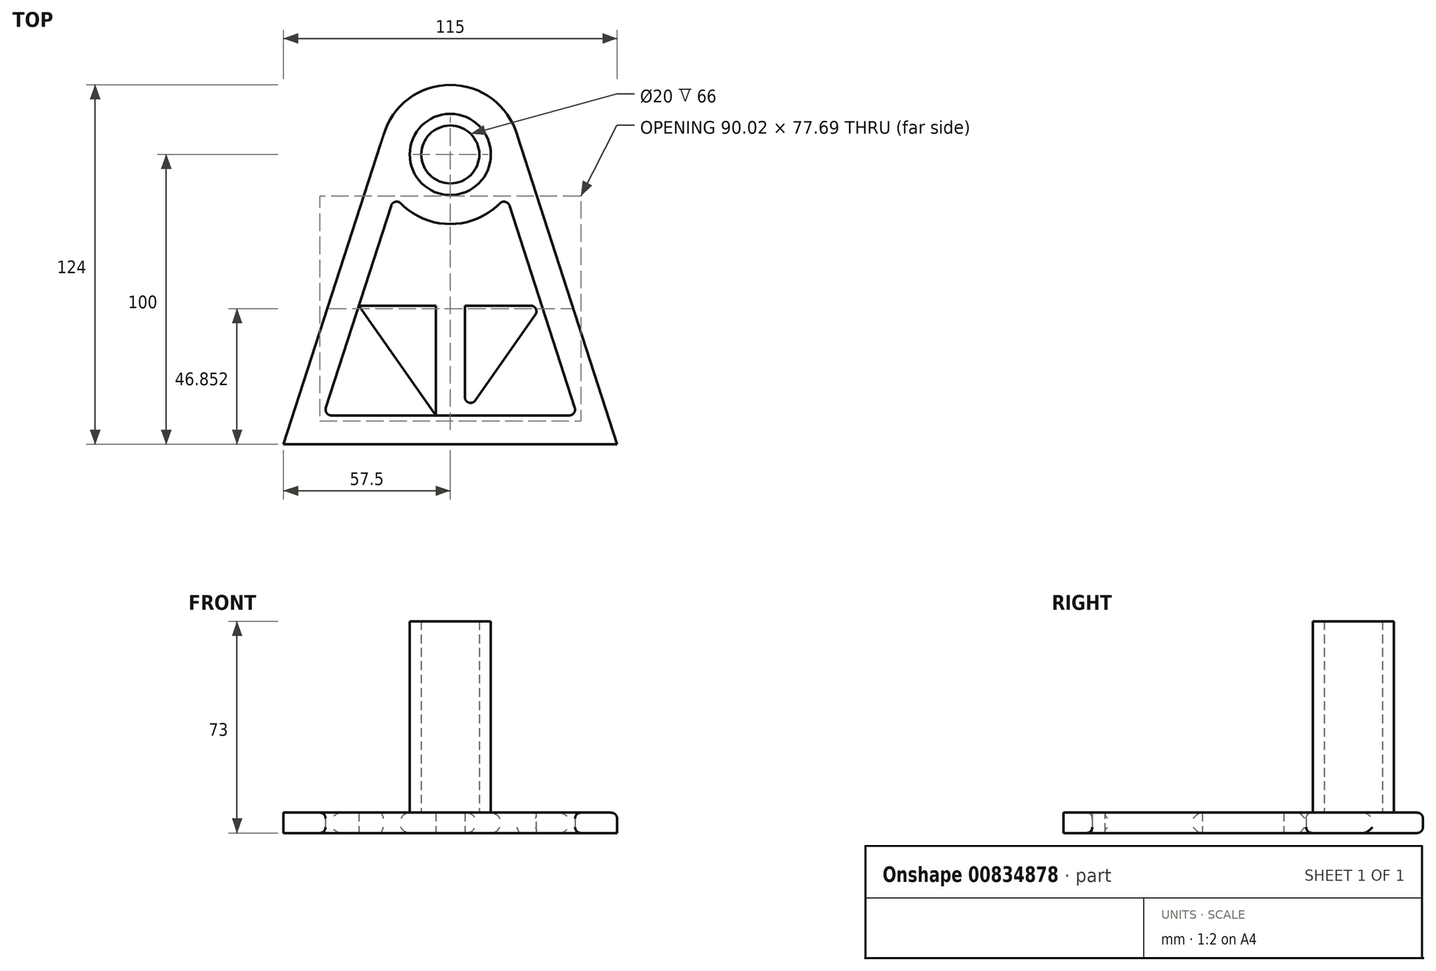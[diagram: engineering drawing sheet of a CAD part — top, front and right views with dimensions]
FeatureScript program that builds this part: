
annotation { "Feature Type Name" : "Feature", "Feature Type Description" : "" }
export const myFeature = defineFeature(function(context is Context, id is Id, definition is map)
    precondition{}
    {
        {
            var Q0;
            Q0=qCreatedBy(makeId("Top.planeOp"),FACE);
            var sketch = newSketch(context, id + "F0", { "sketchPlane" : qUnion([Q0])});
            skCircle(sketch, "E0", {"center": v(0, 0) * mm, "radius": 14 * mm});
            skLineSegment(sketch, "E1", {"start": v(0, 0) * mm, "end": v(0, -100) * mm});
            skCircle(sketch, "E2", {"center": v(0, 0) * mm, "radius": 24 * mm});
            skLineSegment(sketch, "E3", {"start": v(0, -100) * mm, "end": v(-57.5, -100) * mm});
            skLineSegment(sketch, "E4", {"start": v(-57.5, -100) * mm, "end": v(57.5, -100) * mm});
            skLineSegment(sketch, "E5", {"start": v(-23.06, 6.66) * mm, "end": v(-57.5, -100) * mm});
            skLineSegment(sketch, "E6", {"start": v(23.06, 6.66) * mm, "end": v(57.5, -100) * mm});
            skCircle(sketch, "E7", {"center": v(0, 0) * mm, "radius": 10 * mm});
            skLineSegment(sketch, "E8", {"start": v(24.7, -100) * mm, "end": v(24.7, -90) * mm});
            skLineSegment(sketch, "E9", {"start": v(24.7, -90) * mm, "end": v(-43.76, -90) * mm});
            skLineSegment(sketch, "E10", {"start": v(-43.76, -90) * mm, "end": v(-53.28, -86.93) * mm});
            skLineSegment(sketch, "E11", {"start": v(-43.76, -90) * mm, "end": v(-43.76, -100) * mm});
            skLineSegment(sketch, "E12", {"start": v(-43.76, -100) * mm, "end": v(-43.76, -90) * mm});
            skLineSegment(sketch, "E13", {"start": v(-43.76, -90) * mm, "end": v(-19.3, -14.26) * mm});
            skLineSegment(sketch, "E14", {"start": v(24.7, -90) * mm, "end": v(43.76, -90) * mm});
            skLineSegment(sketch, "E15", {"start": v(43.76, -90) * mm, "end": v(53.28, -86.93) * mm});
            skLineSegment(sketch, "E16", {"start": v(43.76, -90) * mm, "end": v(19.3, -14.26) * mm});
            skLineSegment(sketch, "E17", {"start": v(-19.83, -15.9) * mm, "end": v(-29.35, -12.82) * mm});
            skLineSegment(sketch, "E18", {"start": v(0, -90) * mm, "end": v(-5, -90) * mm});
            skLineSegment(sketch, "E19", {"start": v(-5, -90) * mm, "end": v(-31.53, -52.13) * mm});
            skLineSegment(sketch, "E20", {"start": v(0, -90) * mm, "end": v(5, -90) * mm});
            skLineSegment(sketch, "E21", {"start": v(5, -90) * mm, "end": v(31.53, -52.13) * mm});
            skLineSegment(sketch, "E22", {"start": v(5, -90) * mm, "end": v(5, -52.13) * mm});
            skLineSegment(sketch, "E23", {"start": v(-5, -52.13) * mm, "end": v(-5, -90) * mm});
            skLineSegment(sketch, "E24", {"start": v(-5, -52.13) * mm, "end": v(-31.53, -52.13) * mm});
            skLineSegment(sketch, "E25", {"start": v(5, -52.13) * mm, "end": v(31.53, -52.13) * mm});
            skLineSegment(sketch, "E26", {"start": v(-5, -42.32) * mm, "end": v(-28.37, -42.32) * mm});
            skLineSegment(sketch, "E27", {"start": v(5, -41.98) * mm, "end": v(28.26, -41.98) * mm});
            skLineSegment(sketch, "E28", {"start": v(5, -41.98) * mm, "end": v(5, -23.47) * mm});
            skLineSegment(sketch, "E29", {"start": v(-5, -42.32) * mm, "end": v(-5, -23.47) * mm});
            skSolve(sketch);
        }
        {
            var Q0;
            Q0 = qSketchRegion(id + "F0", true);
            var Q1;
            Q1=makeQuery(id+"F0.imprint","IMPRINT",FACE,{"disambiguationData":[TD([[makeQuery(id+"F0.imprint","IMPRINT",EDGE,{"derivedFrom":sQuery(id+"F0.wireOp",EDGE,"E19")}),-1.0]])]});
            var Q2;
            Q2=makeQuery(id+"F0.imprint","IMPRINT",FACE,{"disambiguationData":[TD([[makeQuery(id+"F0.imprint","IMPRINT",EDGE,{"derivedFrom":sQuery(id+"F0.wireOp",EDGE,"E21")}),1.0]])]});
            var Q3;
            {var subQ0=sQuery(id+"F0.wireOp",EDGE,"E20");Q3=makeQuery(id+"F0.imprint","IMPRINT",FACE,{"disambiguationData":[TD([[makeQuery(id+"F0.imprint","IMPRINT",EDGE,{"derivedFrom":subQ0}),1.0]])]});}
            var Q4;
            {var subQ0=sQuery(id+"F0.wireOp",EDGE,"E18");Q4=makeQuery(id+"F0.imprint","IMPRINT",FACE,{"disambiguationData":[TD([[makeQuery(id+"F0.imprint","IMPRINT",EDGE,{"derivedFrom":subQ0}),-1.0]])]});}
            var Q5;
            Q5=makeQuery(id+"F0.imprint","IMPRINT",FACE,{"disambiguationData":[TD([[makeQuery(id+"F0.imprint","IMPRINT",EDGE,{"derivedFrom":sQuery(id+"F0.wireOp",EDGE,"E7")}),1.0]])]});
            var Q6;
            Q6=makeQuery(id+"F0.imprint","IMPRINT",FACE,{"disambiguationData":[TD([[makeQuery(id+"F0.imprint","IMPRINT",EDGE,{"derivedFrom":sQuery(id+"F0.wireOp",EDGE,"E0")}),1.0]])]});
            extrude(context, id + "F1", {"entities" : qUnion([Q0, Q1, Q2, Q3, Q4, Q5, Q6]), "depth" : 7 * mm, "offsetDistance" : 25 * mm});
        }
        {
            var Q0;
            Q0=makeQuery(id+"F0.imprint","IMPRINT",FACE,{"disambiguationData":[TD([[makeQuery(id+"F0.imprint","IMPRINT",EDGE,{"derivedFrom":sQuery(id+"F0.wireOp",EDGE,"E0")}),1.0]])]});
            extrude(context, id + "F2", {"entities" : qUnion([Q0]), "operationType" : NewBodyOperationType.ADD, "depth" : 73 * mm, "offsetDistance" : 25 * mm});
        }
        {
            var Q0;
            Q0=makeQuery(id+"F1.opExtrude","CAP_EDGE",EDGE,{"disambiguationData":[OSD([sQuery(id+"F0.wireOp",EDGE,"E28")])],"isStart":false});
            var Q1;
            {var subQ0=sQuery(id+"F0.wireOp",EDGE,"E13");var subQ1=makeQuery(id+"F0.imprint","INTERSECT",VERTEX,{"derivedFrom":[subQ0,sQuery(id+"F0.wireOp",EDGE,"E17")]});Q1=makeQuery(id+"F1.opExtrude","SWEPT_FACE",FACE,{"disambiguationData":[OSD([subQ0]),TDD([makeQuery(id+"F0.imprint","IMPRINT",EDGE,{"disambiguationData":[TD([[subQ1,1.0]])],"derivedFrom":subQ0}),makeQuery(id+"F0.imprint","IMPRINT",EDGE,{"disambiguationData":[TD([[makeQuery(id+"F0.imprint","INTERSECT",VERTEX,{"derivedFrom":[sQuery(id+"F0.wireOp",EDGE,"E2"),subQ0]}),1.0]])],"derivedFrom":subQ0})])]});}
            var Q2;
            Q2=makeQuery(id+"F1.opExtrude","SWEPT_FACE",FACE,{"disambiguationData":[OSD([sQuery(id+"F0.wireOp",EDGE,"E28")])]});
            var Q3;
            {var subQ0=sQuery(id+"F0.wireOp",EDGE,"E13");Q3=makeQuery(id+"F1.opExtrude","SWEPT_FACE",FACE,{"disambiguationData":[OSD([subQ0]),TDD([makeQuery(id+"F0.imprint","IMPRINT",EDGE,{"disambiguationData":[TD([[makeQuery(id+"F0.imprint","INTERSECT",VERTEX,{"derivedFrom":[subQ0,sQuery(id+"F0.wireOp",EDGE,"E19"),sQuery(id+"F0.wireOp",EDGE,"E24")]}),1.0]])],"derivedFrom":subQ0})])]});}
            var Q4;
            Q4=makeQuery(id+"F1.opExtrude","SWEPT_FACE",FACE,{"disambiguationData":[OSD([sQuery(id+"F0.wireOp",EDGE,"E21")])]});
            var Q5;
            Q5=makeQuery(id+"F1.opExtrude","CAP_EDGE",EDGE,{"disambiguationData":[OSD([sQuery(id+"F0.wireOp",EDGE,"E6")])],"isStart":false});
            var Q6;
            {var subQ0=sQuery(id+"F0.wireOp",EDGE,"E2");Q6=makeQuery(id+"F1.opExtrude","SWEPT_FACE",FACE,{"disambiguationData":[OSD([subQ0]),TDD([makeQuery(id+"F0.imprint","IMPRINT",EDGE,{"disambiguationData":[TD([[makeQuery(id+"F0.imprint","INTERSECT",VERTEX,{"derivedFrom":[subQ0,sQuery(id+"F0.wireOp",EDGE,"E5")]}),1.0]])],"derivedFrom":subQ0})])]});}
            var Q7;
            Q7=makeQuery(id+"F1.opExtrude","SWEPT_FACE",FACE,{"disambiguationData":[OSD([sQuery(id+"F0.wireOp",EDGE,"E29")])]});
            var Q8;
            {var subQ0=sQuery(id+"F0.wireOp",EDGE,"E16");Q8=makeQuery(id+"F1.opExtrude","SWEPT_FACE",FACE,{"disambiguationData":[OSD([subQ0]),TDD([makeQuery(id+"F0.imprint","IMPRINT",EDGE,{"disambiguationData":[TD([[makeQuery(id+"F0.imprint","INTERSECT",VERTEX,{"derivedFrom":[sQuery(id+"F0.wireOp",EDGE,"E2"),subQ0]}),1.0]])],"derivedFrom":subQ0})])]});}
            fillet(context, id + "F3", {"entities" : qUnion([Q0, Q1, Q2, Q3, Q4, Q5, Q6, Q7, Q8]), "radius" : 2 * mm, "tangentPropagation" : true, "allowEdgeOverflow" : false});
        }
    });
